# Revit family: PRE030048-FR
name_source: partatom
category: Generic Models
revit_build: Autodesk Revit 2015 (Build: 20140606_1530(x64)
units: mm (PartAtom-declared; Revit-internal decimal feet)

## types (1)
- PRE030048-FR
    Adresse = 7, RUE RACINE - 92542 MONTROUGE CEDEX FRANCE
    Description = Régulateur thermostatique de sécurité 3/4" avec butée de température
    Débit = "Débit d'eau mitigée minimum : 5L/Mn
Débit d'eau mitigée à 3 bar : 57L/Mn"
    Fabricant = LES ROBINETS PRESTO S.A.
    Finition = Corps en laiton
    Finition 1 = <By Category>
    Fonction = Avec butée de température interne et entrées latérales 3/4" (20x27)
    Garantie = 3 ans
    Hauteur = 92 mm
Largeur
    Largeur = 58 mm
    Lien CCTP = http://www.prestodatashare.com
    Lien fiche produit = http://www.prestodatashare.com
    Lien notice d'utilisation = http://www.prestodatashare.com
    Manufacturer URL = http://www.prestodatashare.com
    Polantis code = PRE030048
    Pression = 2 à 5 bars
    Profondeur = 112 mm
    Raccordement = G3/4"
    Référence = 29002
    URL = http://www.prestodatashare.com

## geometry (parser evidence)
native form markers: Sweep x2
no freeform markers — native parametric forms only
